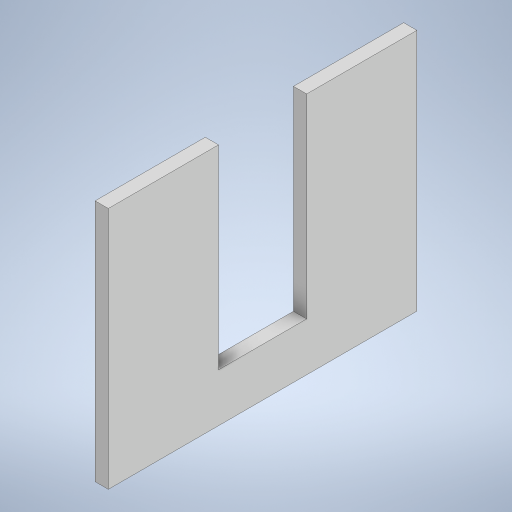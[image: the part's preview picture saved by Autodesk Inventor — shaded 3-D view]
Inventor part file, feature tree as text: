
AUTODESK INVENTOR PART (.ipt)
format: ipt  version: 2023 (Build 270158000, 158)  size: 205,312 bytes
history: native  units: mm
features: extrude x1, sketch x1
ambient origin geometry x8: Origin, YZ Plane, XZ Plane, XY Plane, X Axis, Y Axis, Z Axis, Center Point
bodies: Solid1 (feature_tree)
feature tree (2):
  extrude  "Extrusion1"  Depth=55.175mm
  sketch  "Sketch1"  dims[d0=70.0mm d4=55.175mm d5=25.0mm d6=44.2mm d7=20.0mm d8=25.0mm d9=3.0mm d10=0.0mm]
